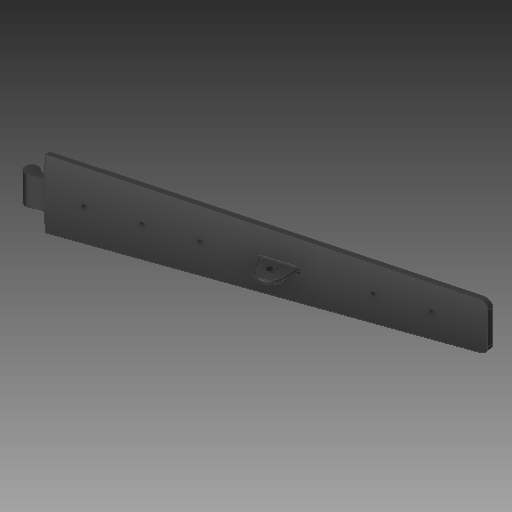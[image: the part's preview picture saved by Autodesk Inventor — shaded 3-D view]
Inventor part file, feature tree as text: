
AUTODESK INVENTOR PART (.ipt)
format: ipt  version: 2019 (Build 230136000, 136)  size: 355,840 bytes
history: native  units: mm
features: other x3, fillet x3, move_body x2, direct_edit x1, plane x1
ambient origin geometry x8: Origin, YZ Plane, XZ Plane, XY Plane, X Axis, Y Axis, Z Axis, Center Point
bodies: Solid1 (feature_tree)
feature tree (10):
  other  "BladeSkeleton.ipt"
  direct_edit  "Direct Edit1"
  fillet  "Fillet2"  Radius=10.0mm
  fillet  "Fillet3"  [1 undecoded]
  fillet  "Fillet4"  [1 undecoded]
  plane  "Work Plane3"
  other  "Solid4::BladeSkeleton.ipt"
  other  "TaggingFeature1"
  move_body  "Move1"
  move_body  "Move2"
note: 2 required parameter values undecoded (feature->parameter linkage not recoverable at this tier; creation-order binding heuristic only, values carry confidence <= 0.55)
